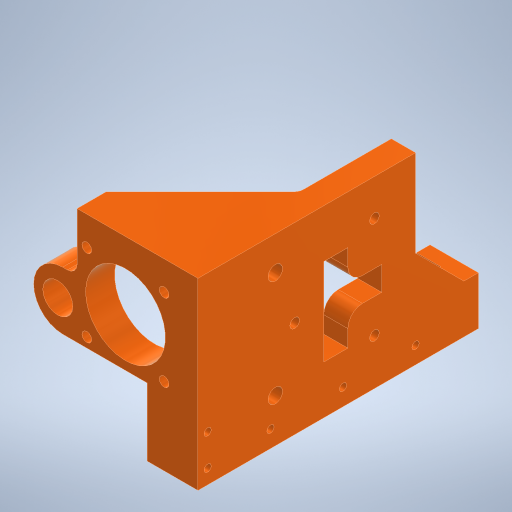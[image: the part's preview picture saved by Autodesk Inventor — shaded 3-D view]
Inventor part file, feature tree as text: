
AUTODESK INVENTOR PART (.ipt)
format: ipt  version: 2024.1 (Build 281209000, 209)  size: 499,200 bytes
history: native  units: in
note: dims shown in document units (in); Inventor stores cm internally (conversion verified against a paired STEP export)
features: extrude x18, sketch x18, chamfer x5, fillet x4, mirror x1
ambient origin geometry x8: Origin, YZ Plane, XZ Plane, XY Plane, X Axis, Y Axis, Z Axis, Center Point
bodies: Solid1 (feature_tree)
feature tree (46):
  extrude  "Extrusion1"  Depth=1.4961in
  extrude  "Extrusion2"  Depth=0.9449in
  extrude  "Extrusion3"  Depth=0.7874in TaperAngle=0.0deg
  extrude  "Extrusion4"  Depth=0.3937in
  extrude  "Extrusion5"  Depth=0.0787in
  fillet  "Fillet1"  Radius=0.0787in
  extrude  "Extrusion6"  Depth=0.0787in
  extrude  "Extrusion7"  Depth=0.315in
  chamfer  "Chamfer1"  [1 undecoded]
  chamfer  "Chamfer2"  Distance=0.7874in
  extrude  "Extrusion8"  Depth=0.0787in
  chamfer  "Chamfer3"  [1 undecoded]
  extrude  "Extrusion9"  Depth=0.1181in
  chamfer  "Chamfer4"  Distance=0.1181in
  extrude  "Extrusion10"  Depth=0.1575in
  extrude  "Extrusion15"  Depth=0.0787in
  extrude  "Extrusion16"  Depth=0.0787in
  extrude  "Extrusion17"  Depth=0.1575in
  extrude  "Extrusion18"  TaperAngle=0.0deg  [1 undecoded]
  extrude  "Extrusion19"  Depth=0.0591in TaperAngle=45.0deg
  chamfer  "Chamfer5"  Distance=0.0787in Angle=45.0deg
  extrude  "Extrusion20"  Depth=1.1024in
  extrude  "Extrusion21"  Depth=0.3937in
  fillet  "Fillet3"  [1 undecoded]
  extrude  "Extrusion22"  Depth=0.3937in TaperAngle=45.0deg
  fillet  "Fillet5"  Radius=0.0787in
  fillet  "Fillet6"  Radius=0.0787in
  mirror  "Mirror1"
  sketch  "Sketch1"  dims[d0=1.4961in d1=2.1654in]
  sketch  "Sketch2"  dims[d2=0.1969in d3=0.0in d4=0.9449in]
  sketch  "Sketch3"  dims[d5=0.2362in d6=0.7874in d7=0.0in]
  sketch  "Sketch4"  dims[d8=0.6496in d9=0.3937in]
  sketch  "Sketch5"  dims[d10=0.3937in d11=0.0787in d12=0.0787in]
  sketch  "Sketch6"  dims[d13=0.0787in d14=0.0787in]
  sketch  "Sketch7"  dims[d15=0.315in d16=0.315in]
  sketch  "Sketch8"  dims[d17=0.315in]
  sketch  "Sketch9"  dims[d18=0.315in]
  sketch  "Sketch10"  dims[d19=0.315in]
  sketch  "Sketch15"  dims[d20=0.315in]
  sketch  "Sketch16"  dims[d21=0.315in]
  sketch  "Sketch17"  dims[d22=0.315in d23=0.0in d24=0.0in]
  sketch  "Sketch18"  dims[d25=0.1181in d26=0.7874in d27=0.0in]
  sketch  "Sketch19"  dims[d28=0.0in d29=0.0in d30=0.0787in]
  sketch  "Sketch20"  dims[d31=0.0787in]
  sketch  "Sketch21"  dims[d32=0.7087in]
  sketch  "Sketch22"  dims[d33=1.378in d34=0.0in d35=0.0in d36=0.1181in d37=0.1181in d38=0.1575in d39=0.4331in d40=0.4331in d41=0.1575in d42=0.0in d43=0.0in d44=0.0591in d45=0.0787in d46=45.0deg d47=0.0748in d48=0.0787in d49=45.0deg d50=1.1024in d51=0.3937in d52=0.0in d53=0.0in d54=0.3937in d55=0.0787in d56=45.0deg d57=0.0787in d58=0.0787in d59=0.2953in d60=0.7283in d61=0.374in d62=0.7283in d63=0.0in d64=0.0in d65=0.0591in d66=0.0787in d67=45.0deg d68=0.0591in d69=0.0591in d70=0.0591in d71=0.1378in d72=0.3937in d73=0.1378in d74=0.5906in d76=0.1378in d77=0.0in d78=0.0in d95=0.5906in d96=0.1181in d97=0.3937in d98=0.2165in d99=0.0in d100=0.1102in d101=0.1969in d102=0.0in d103=0.189in d104=0.2165in d105=0.0in d106=0.0591in d107=0.0591in d108=0.2559in d109=0.1181in d110=0.0787in d111=0.0787in d112=0.0in d113=0.0in d114=0.1969in d115=0.3937in d116=0.3937in d117=0.5512in d118=0.0in d119=0.0in d120=0.0197in d121=0.0787in d122=45.0deg d123=0.4724in d124=0.3543in d125=0.0in d126=0.2441in d127=0.2362in d128=0.1969in d129=0.0in d130=0.0in d132=0.2362in d134=0.1969in d135=0.2559in d136=0.2756in d137=0.0in d138=0.0in d139=0.1181in d152=0.0787in]
note: 4 required parameter values undecoded (feature->parameter linkage not recoverable at this tier; creation-order binding heuristic only, values carry confidence <= 0.55)
